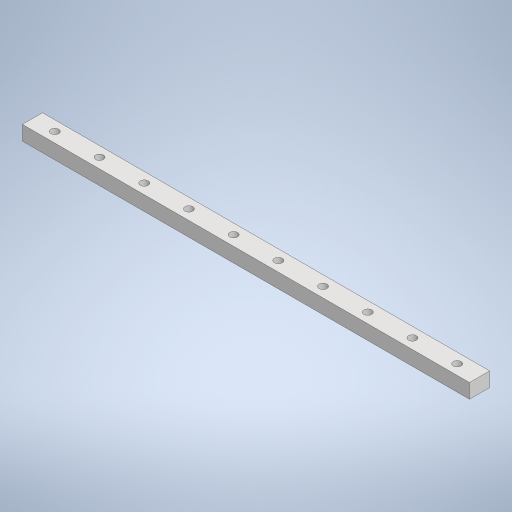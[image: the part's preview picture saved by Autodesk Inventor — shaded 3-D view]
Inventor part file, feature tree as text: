
AUTODESK INVENTOR PART (.ipt)
format: ipt  version: 2024.1 (Build 281209000, 209)  size: 256,000 bytes
history: native  units: in
note: dims shown in document units (in); Inventor stores cm internally (conversion verified against a paired STEP export)
features: extrude x2, sketch x2
ambient origin geometry x8: Origin, YZ Plane, XZ Plane, XY Plane, X Axis, Y Axis, Z Axis, Center Point
bodies: Solid1 (feature_tree)
feature tree (4):
  extrude  "Extrusion1"  Depth=0.3543in
  extrude  "Extrusion2"  Depth=0.3937in
  sketch  "Sketch1"  dims[d0=7.874in d1=0.3543in]
  sketch  "Sketch2"  dims[d2=0.2559in d3=0.0in d4=0.1378in d5=0.1772in d6=0.3937in d7=3.937in d9=0.7874in d10=0.3937in d12=0.3937in d14=0.0in d15=0.0in]
